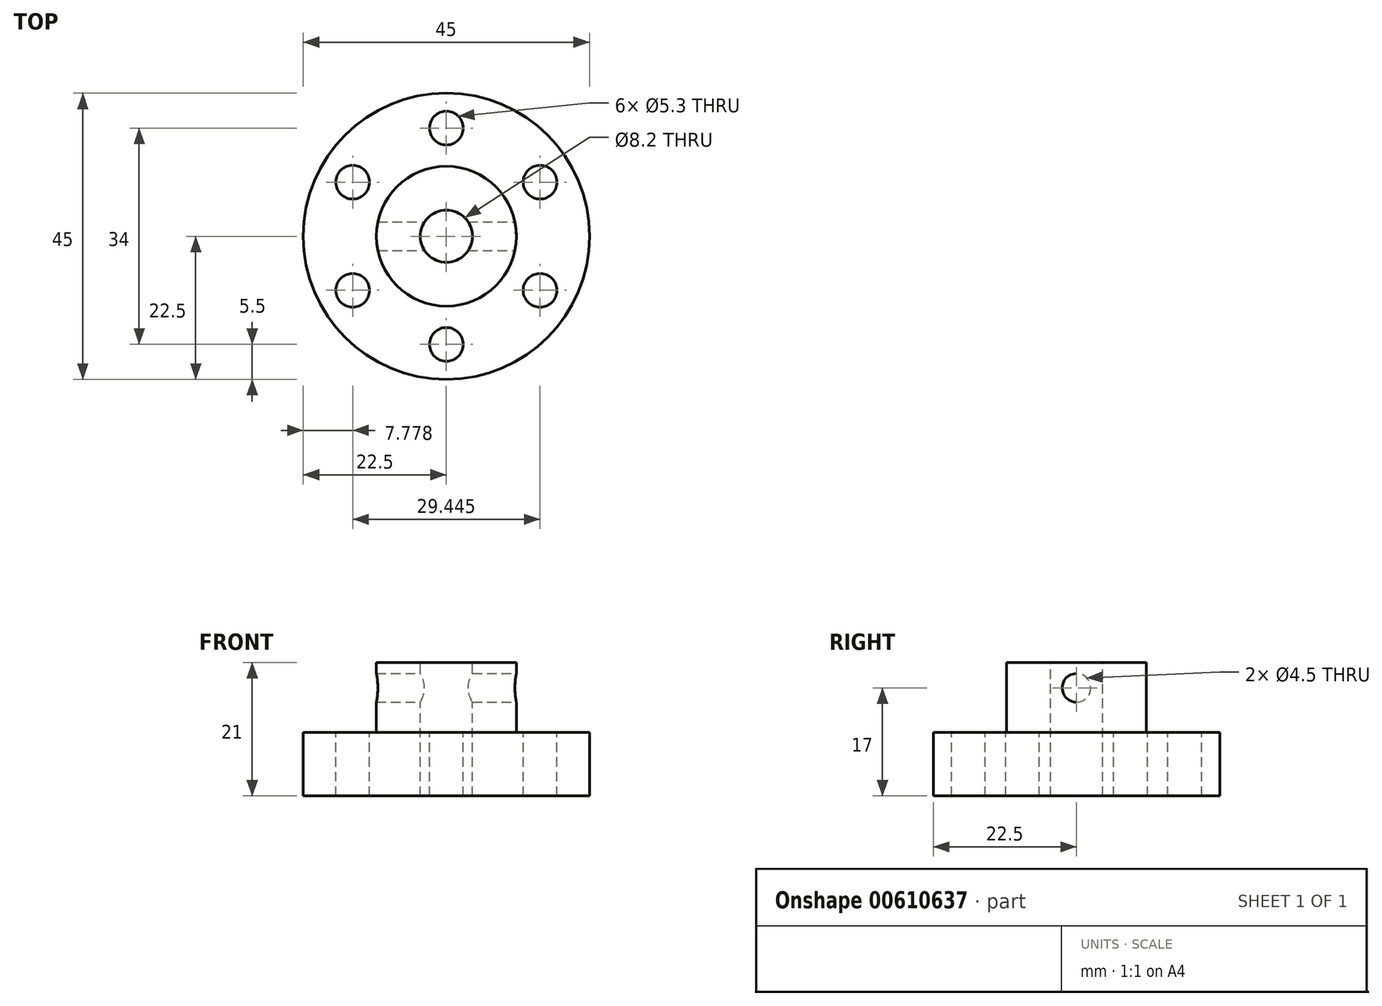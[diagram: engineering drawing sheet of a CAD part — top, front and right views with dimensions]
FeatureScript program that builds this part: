
annotation { "Feature Type Name" : "Feature", "Feature Type Description" : "" }
export const myFeature = defineFeature(function(context is Context, id is Id, definition is map)
    precondition{}
    {
        {
            var Q0;
            Q0=qCreatedBy(makeId("Top.planeOp"),FACE);
            var sketch = newSketch(context, id + "F0", { "sketchPlane" : qUnion([Q0])});
            skCircle(sketch, "E0", {"center": v(0, 0) * mm, "radius": 22.5 * mm});
            skSolve(sketch);
        }
        {
            var Q0;
            Q0=makeQuery(id+"F0.imprint","IMPRINT",FACE,{"disambiguationData":[TD([[makeQuery(id+"F0.imprint","IMPRINT",EDGE,{"derivedFrom":sQuery(id+"F0.wireOp",EDGE,"E0")}),1.0]])]});
            extrude(context, id + "F1", {"entities" : qUnion([Q0]), "depth" : 10 * mm, "offsetDistance" : 25 * mm});
        }
        {
            var Q0;
            Q0=makeQuery(id+"F1.opExtrude","CAP_FACE",FACE,{"disambiguationData":[OSD([sQuery(id+"F0.wireOp",EDGE,"E0")])],"isStart":false});
            var sketch = newSketch(context, id + "F2", { "sketchPlane" : qUnion([Q0])});
            skCircle(sketch, "E1", {"center": v(0, 0) * mm, "radius": 11 * mm});
            skSolve(sketch);
        }
        {
            var Q0;
            Q0=makeQuery(id+"F2.imprint","IMPRINT",FACE,{"disambiguationData":[TD([[makeQuery(id+"F2.imprint","IMPRINT",EDGE,{"derivedFrom":sQuery(id+"F2.wireOp",EDGE,"E1")}),1.0]])]});
            extrude(context, id + "F3", {"entities" : qUnion([Q0]), "operationType" : NewBodyOperationType.ADD, "depth" : 11 * mm, "offsetDistance" : 25 * mm});
        }
        {
            var Q0;
            Q0=makeQuery(id+"F3.opExtrude","CAP_FACE",FACE,{"disambiguationData":[OSD([sQuery(id+"F2.wireOp",EDGE,"E1")])],"isStart":false});
            var sketch = newSketch(context, id + "F4", { "sketchPlane" : qUnion([Q0])});
            skPoint(sketch, "E2", {"position": v(0, 0) * mm});
            skSolve(sketch);
        }
        {
            var Q0;
            Q0=sQuery(id+"F4.wireOp",VERTEX,"E2");
            var Q1;
            Q1=makeQuery(id+"F1.opExtrude","SWEPT_BODY",BODY,{"disambiguationData":[OSD([sQuery(id+"F0.wireOp",EDGE,"E0")])]});
            hole(context, id + "F5", {"style" : HoleStyle.SIMPLE, "endStyle" : HoleEndStyle.THROUGH, "holeDiameter" : 8.2 * mm, "majorDiameter" : 5 * mm, "tappedDepth" : 12 * mm, "tapClearance" : 3, "locations" : qUnion([Q0]), "scope" : qUnion([Q1])});
        }
        {
            var Q0;
            Q0=makeQuery(id+"F1.opExtrude","CAP_FACE",FACE,{"disambiguationData":[OSD([sQuery(id+"F0.wireOp",EDGE,"E0")])],"isStart":false});
            var sketch = newSketch(context, id + "F6", { "sketchPlane" : qUnion([Q0])});
            skPoint(sketch, "E3", {"position": v(0, 17) * mm});
            skPoint(sketch, "E4.1.0", {"position": v(-14.72, 8.5) * mm});
            skPoint(sketch, "E4.2.0", {"position": v(-14.72, -8.5) * mm});
            skPoint(sketch, "E4.3.0", {"position": v(0, -17) * mm});
            skPoint(sketch, "E4.4.0", {"position": v(14.72, -8.5) * mm});
            skPoint(sketch, "E4.5.0", {"position": v(14.72, 8.5) * mm});
            skPoint(sketch, "E4.center", {"position": v(0, 0) * mm});
            skSolve(sketch);
        }
        {
            var Q0;
            Q0=sQuery(id+"F6.wireOp",VERTEX,"E3");
            var Q1;
            Q1=sQuery(id+"F6.wireOp",VERTEX,"E4.5.0");
            var Q2;
            Q2=sQuery(id+"F6.wireOp",VERTEX,"E4.4.0");
            var Q3;
            Q3=sQuery(id+"F6.wireOp",VERTEX,"E4.3.0");
            var Q4;
            Q4=sQuery(id+"F6.wireOp",VERTEX,"E4.2.0");
            var Q5;
            Q5=sQuery(id+"F6.wireOp",VERTEX,"E4.1.0");
            var Q6;
            Q6=makeQuery(id+"F1.opExtrude","SWEPT_BODY",BODY,{"disambiguationData":[OSD([sQuery(id+"F0.wireOp",EDGE,"E0")])]});
            hole(context, id + "F7", {"style" : HoleStyle.SIMPLE, "endStyle" : HoleEndStyle.THROUGH, "holeDiameter" : 5.3 * mm, "majorDiameter" : 5 * mm, "tappedDepth" : 12 * mm, "tapClearance" : 3, "locations" : qUnion([Q0, Q1, Q2, Q3, Q4, Q5]), "scope" : qUnion([Q6])});
        }
        {
            var Q0;
            Q0=qCreatedBy(makeId("Right.planeOp"),FACE);
            var sketch = newSketch(context, id + "F8", { "sketchPlane" : qUnion([Q0])});
            skCircle(sketch, "E5", {"center": v(0, 17) * mm, "radius": 2.25 * mm});
            skSolve(sketch);
        }
        {
            var Q0;
            Q0=qSketchRegion(id+"F8",true);
            extrude(context, id + "F9", {"entities" : qUnion([Q0]), "operationType" : NewBodyOperationType.REMOVE, "endBound" : BoundingType.SYMMETRIC, "oppositeDirection" : true, "depth" : 100 * mm, "offsetDistance" : 25 * mm});
        }
    });
